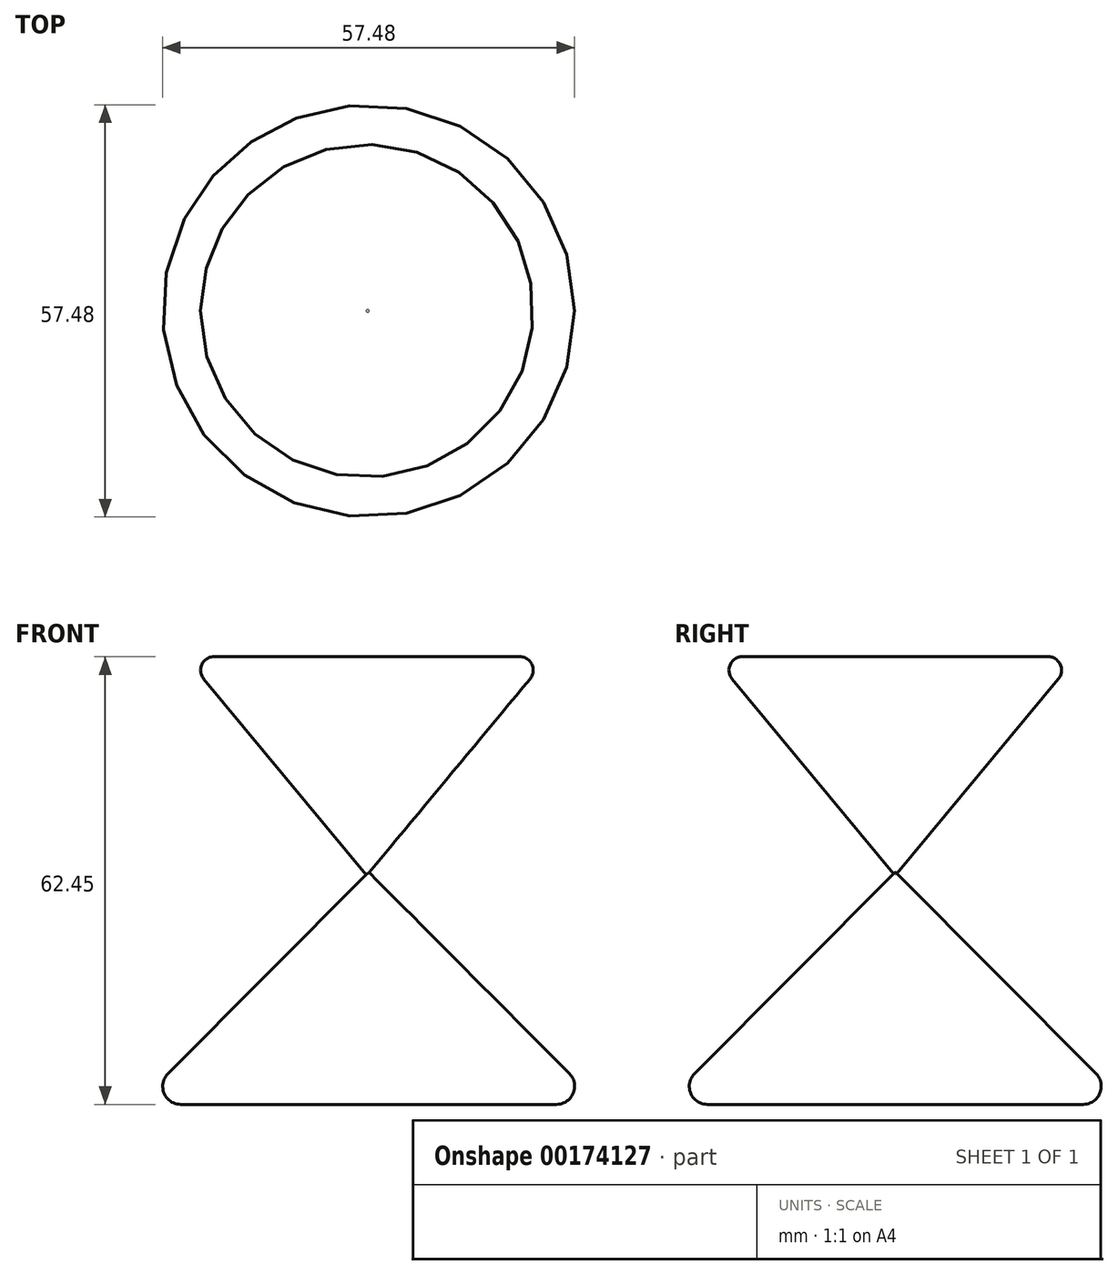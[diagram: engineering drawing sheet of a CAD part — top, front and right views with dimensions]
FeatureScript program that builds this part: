
annotation { "Feature Type Name" : "Feature", "Feature Type Description" : "" }
export const myFeature = defineFeature(function(context is Context, id is Id, definition is map)
    precondition{}
    {
        {
            var Q0;
            Q0=qCreatedBy(makeId("Front.planeOp"),FACE);
            var sketch = newSketch(context, id + "F0", { "sketchPlane" : qUnion([Q0])});
            skLineSegment(sketch, "E0", {"start": v(-44.37, 32.41) * mm, "end": v(-44.37, 0) * mm});
            skLineSegment(sketch, "E1", {"start": v(-44.37, 0) * mm, "end": v(-12.07, 0) * mm});
            skLineSegment(sketch, "E2", {"start": v(-12.07, 0) * mm, "end": v(-44.37, 32.41) * mm});
            skSolve(sketch);
        }
        {
            var Q0;
            Q0 = qSketchRegion(id + "F0", true);
            var Q1;
            Q1=sQuery(id+"F0.wireOp",EDGE,"E0");
            revolve(context, id + "F1", {"entities" : qUnion([Q0]), "axis" : qUnion([Q1]), "revolveType" : RevolveType.FULL});
        }
        {
            var Q0;
            Q0=makeQuery(id+"F1.opRevolve","SWEPT_EDGE",EDGE,{"disambiguationData":[OSD([sQuery(id+"F0.wireOp",EDGE,"E1"),sQuery(id+"F0.wireOp",EDGE,"E2")])]});
            var Q1;
            Q1=makeQuery(id+"F1.opRevolve","SWEPT_FACE",FACE,{"disambiguationData":[OSD([sQuery(id+"F0.wireOp",EDGE,"E2")])]});
            fillet(context, id + "F2", {"entities" : qUnion([Q0, Q1]), "radius" : 2.53 * mm, "tangentPropagation" : true, "allowEdgeOverflow" : false});
        }
        {
            var Q0;
            Q0=qCreatedBy(makeId("Front.planeOp"),FACE);
            var sketch = newSketch(context, id + "F3", { "sketchPlane" : qUnion([Q0])});
            skLineSegment(sketch, "E3", {"start": v(-44.6, 31.95) * mm, "end": v(-44.6, 62.45) * mm});
            skLineSegment(sketch, "E4", {"start": v(-44.6, 62.45) * mm, "end": v(-19.28, 62.45) * mm});
            skLineSegment(sketch, "E5", {"start": v(-19.28, 62.45) * mm, "end": v(-44.6, 31.95) * mm});
            skSolve(sketch);
        }
        {
            var Q0;
            Q0 = qSketchRegion(id + "F3", true);
            var Q1;
            Q1=sQuery(id+"F3.wireOp",EDGE,"E3");
            revolve(context, id + "F4", {"operationType" : NewBodyOperationType.ADD, "entities" : qUnion([Q0]), "axis" : qUnion([Q1]), "revolveType" : RevolveType.FULL});
        }
        {
            var Q0;
            Q0=makeQuery(id+"F4.opRevolve","SWEPT_FACE",FACE,{"disambiguationData":[OSD([sQuery(id+"F3.wireOp",EDGE,"E4")])]});
            fillet(context, id + "F5", {"entities" : qUnion([Q0]), "radius" : 1.88 * mm, "tangentPropagation" : true, "allowEdgeOverflow" : false});
        }
    });
